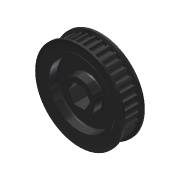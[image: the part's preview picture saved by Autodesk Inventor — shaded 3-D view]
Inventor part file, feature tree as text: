
AUTODESK INVENTOR PART (.ipt)
format: ipt  version: 2013 (Build 170138000, 138)  size: 826,368 bytes
history: native  units: in
note: dims shown in document units (in); Inventor stores cm internally (conversion verified against a paired STEP export)
features: mirror x1, other x1, imported_body x1
ambient origin geometry x8: Origin, YZ Plane, XZ Plane, XY Plane, X Axis, Y Axis, Z Axis, Center Point
feature tree (3):
  mirror  "Mirror1"
  other  "217-3231-STEP1"
  imported_body  "Base1"
